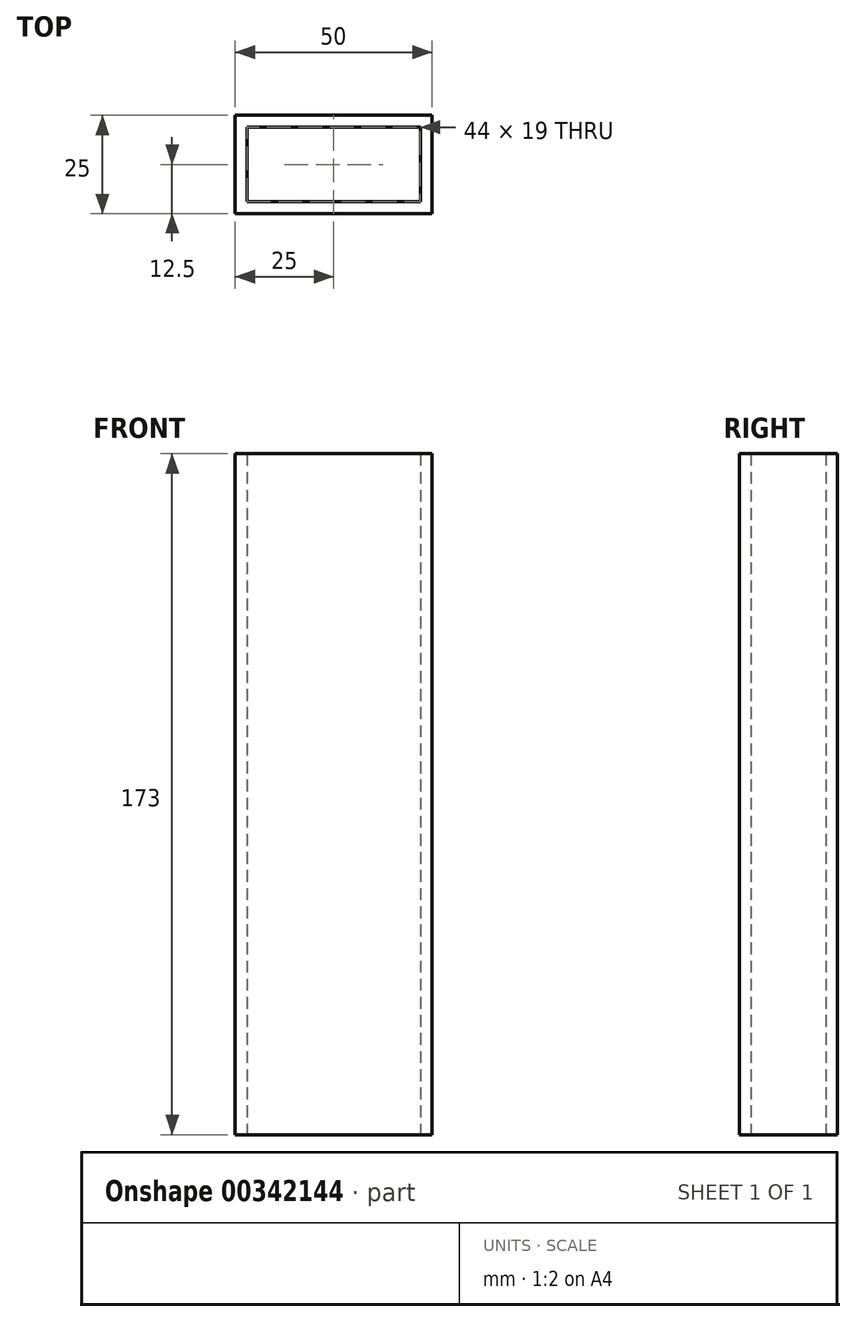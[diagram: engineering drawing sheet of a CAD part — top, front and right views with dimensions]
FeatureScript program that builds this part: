
annotation { "Feature Type Name" : "Feature", "Feature Type Description" : "" }
export const myFeature = defineFeature(function(context is Context, id is Id, definition is map)
    precondition{}
    {
        {
            var Q0;
            Q0=qCreatedBy(makeId("Top.planeOp"),FACE);
            var sketch = newSketch(context, id + "F0", { "sketchPlane" : qUnion([Q0])});
            skLineSegment(sketch, "E0.bottom", {"start": v(-25, -12.5) * mm, "end": v(25, -12.5) * mm});
            skLineSegment(sketch, "E0.top", {"start": v(-25, 12.5) * mm, "end": v(25, 12.5) * mm});
            skLineSegment(sketch, "E0.left", {"start": v(-25, -12.5) * mm, "end": v(-25, 12.5) * mm});
            skLineSegment(sketch, "E0.right", {"start": v(25, -12.5) * mm, "end": v(25, 12.5) * mm});
            skPoint(sketch, "E0.middle", {"position": v(0, 0) * mm});
            skLineSegment(sketch, "E1.bottom", {"start": v(22, -9.5) * mm, "end": v(-22, -9.5) * mm});
            skLineSegment(sketch, "E1.top", {"start": v(22, 9.5) * mm, "end": v(-22, 9.5) * mm});
            skLineSegment(sketch, "E1.left", {"start": v(22, -9.5) * mm, "end": v(22, 9.5) * mm});
            skLineSegment(sketch, "E1.right", {"start": v(-22, -9.5) * mm, "end": v(-22, 9.5) * mm});
            skSolve(sketch);
        }
        {
            var Q0;
            Q0=qSketchRegion(id+"F0",true);
            extrude(context, id + "F1", {"entities" : qUnion([Q0]), "endBound" : BoundingType.SYMMETRIC, "depth" : 173 * mm});
        }
    });
